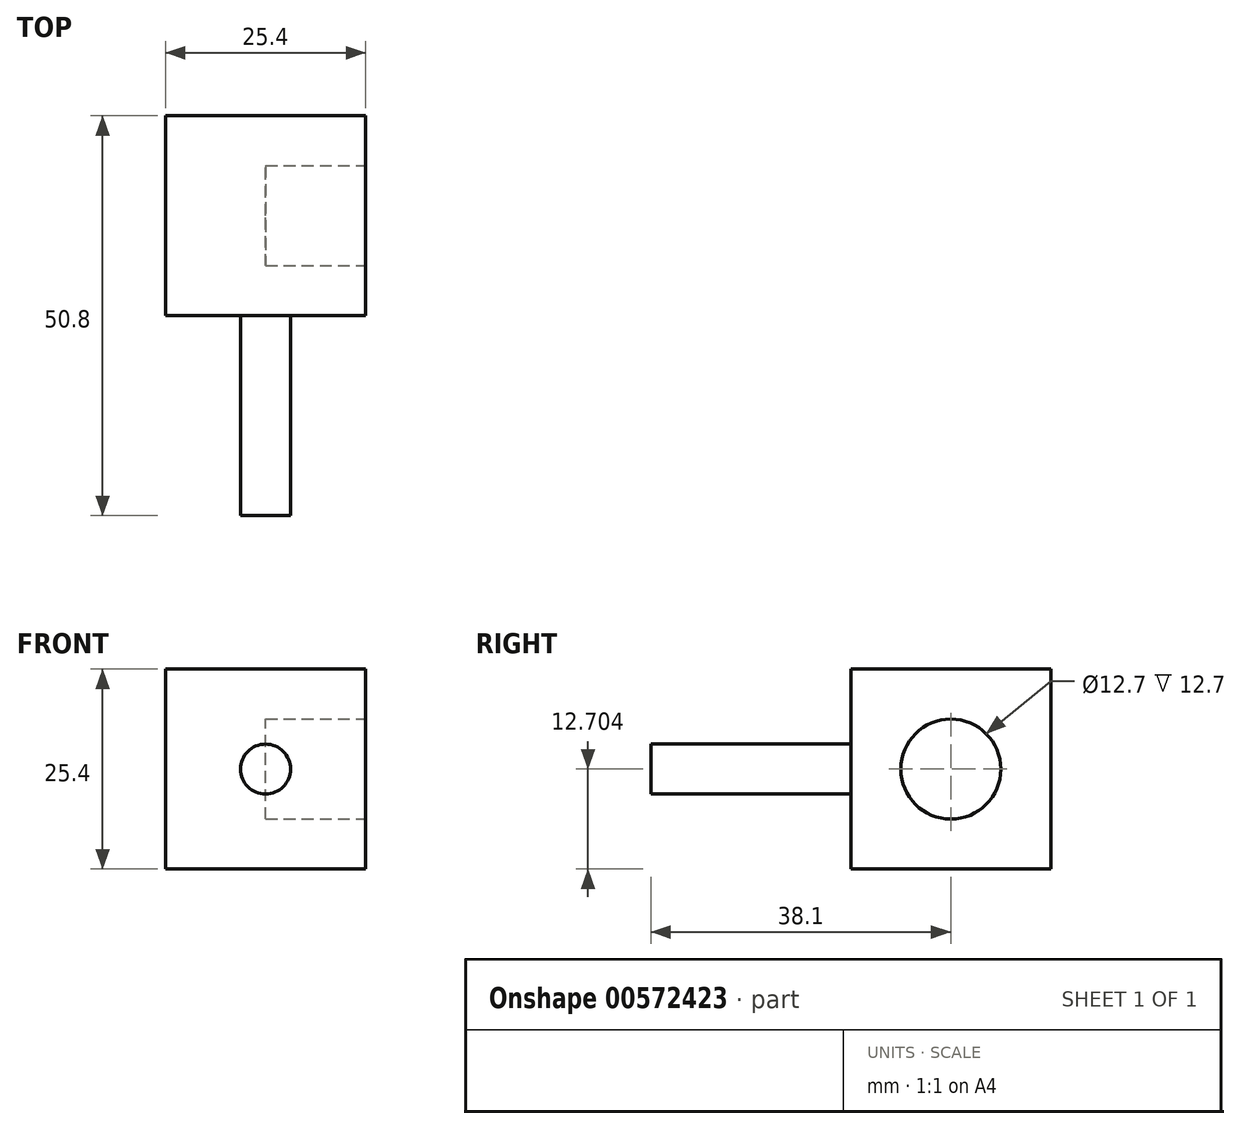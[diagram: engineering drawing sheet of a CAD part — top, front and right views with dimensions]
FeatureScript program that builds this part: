
annotation { "Feature Type Name" : "Feature", "Feature Type Description" : "" }
export const myFeature = defineFeature(function(context is Context, id is Id, definition is map)
    precondition{}
    {
        {
            var Q0;
            Q0=qCreatedBy(makeId("Front.planeOp"),FACE);
            var sketch = newSketch(context, id + "F0", { "sketchPlane" : qUnion([Q0])});
            skLineSegment(sketch, "E0.bottom", {"start": v(-7.13, 3.82) * mm, "end": v(18.27, 3.82) * mm});
            skLineSegment(sketch, "E0.top", {"start": v(-7.13, -21.58) * mm, "end": v(18.27, -21.58) * mm});
            skLineSegment(sketch, "E0.left", {"start": v(-7.13, 3.82) * mm, "end": v(-7.13, -21.58) * mm});
            skLineSegment(sketch, "E0.right", {"start": v(18.27, 3.82) * mm, "end": v(18.27, -21.58) * mm});
            skSolve(sketch);
        }
        {
            var Q0;
            Q0=makeQuery(id+"F0.imprint","IMPRINT",FACE,{"disambiguationData":[TD([[makeQuery(id+"F0.imprint","IMPRINT",EDGE,{"derivedFrom":sQuery(id+"F0.wireOp",EDGE,"E0.bottom")}),-1.0]])]});
            extrude(context, id + "F1", {"entities" : qUnion([Q0]), "depth" : 25.4 * mm, "offsetDistance" : 25.4 * mm});
        }
        {
            var Q0;
            Q0=makeQuery(id+"F1.opExtrude","CAP_FACE",FACE,{"disambiguationData":[OSD([sQuery(id+"F0.wireOp",EDGE,"E0.bottom"),sQuery(id+"F0.wireOp",EDGE,"E0.top"),sQuery(id+"F0.wireOp",EDGE,"E0.left"),sQuery(id+"F0.wireOp",EDGE,"E0.right")])],"isStart":false});
            var sketch = newSketch(context, id + "F2", { "sketchPlane" : qUnion([Q0])});
            skCircle(sketch, "E1", {"center": v(5.57, -8.88) * mm, "radius": 3.18 * mm});
            skSolve(sketch);
        }
        {
            var Q0;
            Q0=makeQuery(id+"F2.imprint","IMPRINT",FACE,{"disambiguationData":[TD([[makeQuery(id+"F2.imprint","IMPRINT",EDGE,{"derivedFrom":sQuery(id+"F2.wireOp",EDGE,"E1")}),1.0]])]});
            extrude(context, id + "F3", {"entities" : qUnion([Q0]), "operationType" : NewBodyOperationType.ADD, "depth" : 25.4 * mm, "offsetDistance" : 25.4 * mm});
        }
        {
            var Q0;
            Q0=makeQuery(id+"F1.opExtrude","SWEPT_FACE",FACE,{"disambiguationData":[OSD([sQuery(id+"F0.wireOp",EDGE,"E0.right")])]});
            var sketch = newSketch(context, id + "F4", { "sketchPlane" : qUnion([Q0])});
            skCircle(sketch, "E2", {"center": v(-12.7, -8.88) * mm, "radius": 6.35 * mm});
            skSolve(sketch);
        }
        {
            var Q0;
            Q0=makeQuery(id+"F4.imprint","IMPRINT",FACE,{"disambiguationData":[TD([[makeQuery(id+"F4.imprint","IMPRINT",EDGE,{"derivedFrom":sQuery(id+"F4.wireOp",EDGE,"E2")}),1.0]])]});
            extrude(context, id + "F5", {"entities" : qUnion([Q0]), "operationType" : NewBodyOperationType.REMOVE, "oppositeDirection" : true, "depth" : 12.7 * mm, "offsetDistance" : 25.4 * mm});
        }
    });
